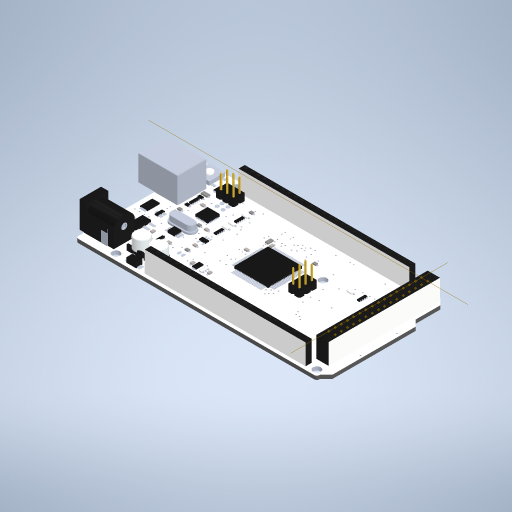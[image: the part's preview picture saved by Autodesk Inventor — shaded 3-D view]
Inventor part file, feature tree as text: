
AUTODESK INVENTOR PART (.ipt)
format: ipt  version: 2023.1 (Build 271208000, 208)  size: 4,338,176 bytes
history: native  units: in
note: dims shown in document units (in); Inventor stores cm internally (conversion verified against a paired STEP export)
features: other x3, fillet x1
ambient origin geometry x8: Origin, YZ Plane, XZ Plane, XY Plane, X Axis, Y Axis, Z Axis, Center Point
bodies: Solid1 (feature_tree)
feature tree (4):
  other  "Work Axis1"
  other  "Work Axis2"
  other  "Work Point7"
  fillet  "Fillet13"  [1 undecoded]
note: 1 required parameter value undecoded (feature->parameter linkage not recoverable at this tier; creation-order binding heuristic only, values carry confidence <= 0.55)
